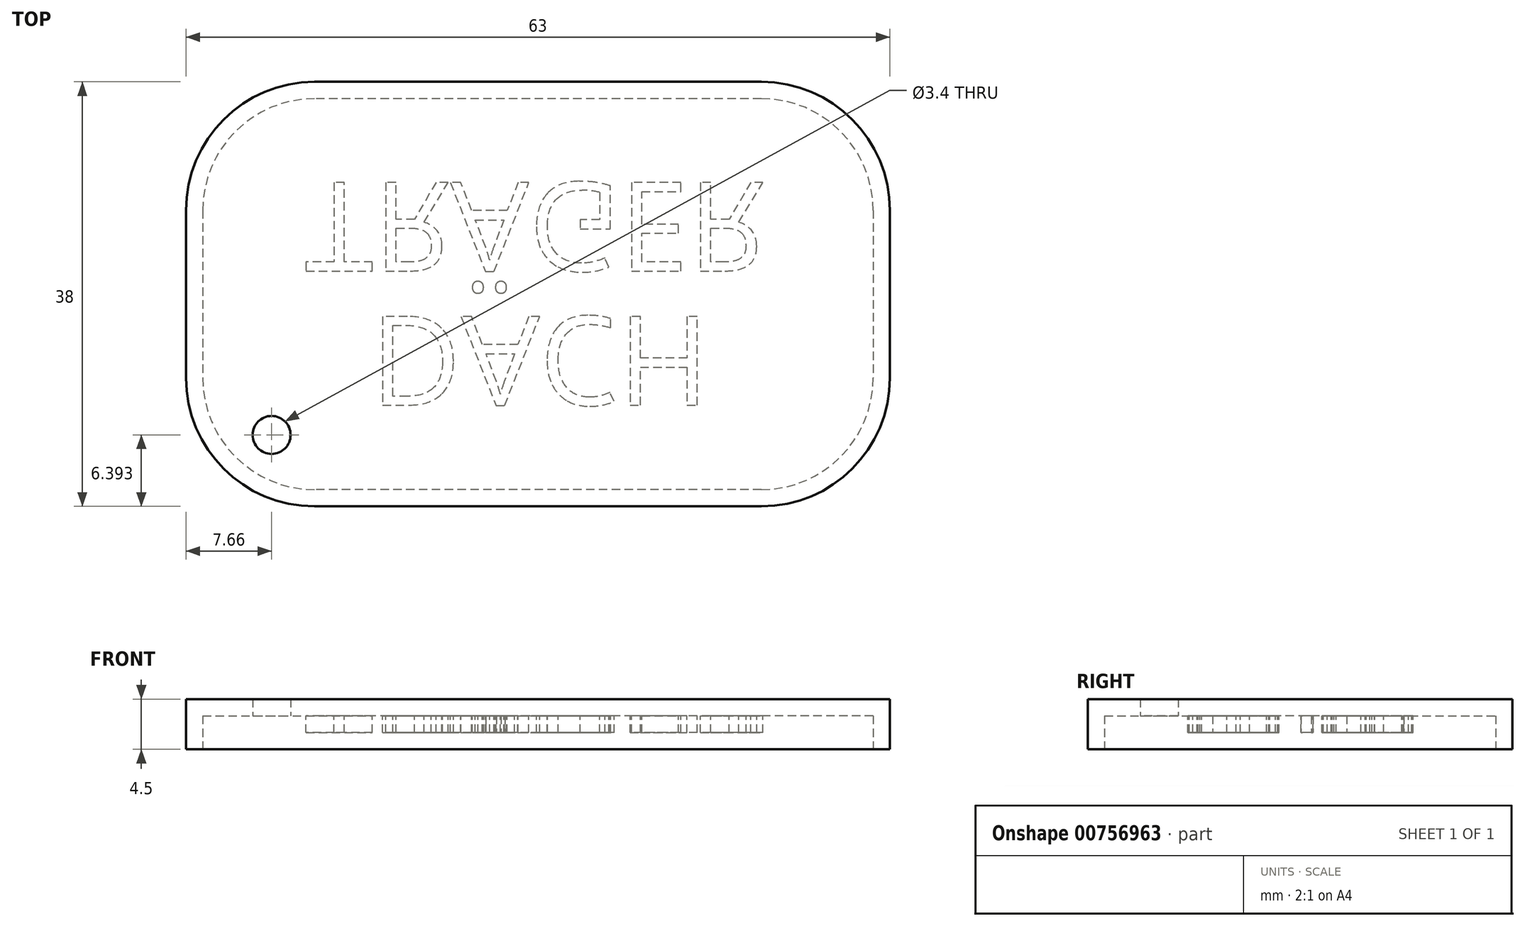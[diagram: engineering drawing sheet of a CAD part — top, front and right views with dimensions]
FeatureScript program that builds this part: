
annotation { "Feature Type Name" : "Feature", "Feature Type Description" : "" }
export const myFeature = defineFeature(function(context is Context, id is Id, definition is map)
    precondition{}
    {
        {
            var Q0;
            Q0=qCreatedBy(makeId("Top.planeOp"),FACE);
            var sketch = newSketch(context, id + "F0", { "sketchPlane" : qUnion([Q0])});
            skLineSegment(sketch, "E0.bottom", {"start": v(30, 17.5) * mm, "end": v(-30, 17.5) * mm});
            skLineSegment(sketch, "E0.top", {"start": v(30, -17.5) * mm, "end": v(-30, -17.5) * mm});
            skLineSegment(sketch, "E0.left", {"start": v(30, 17.5) * mm, "end": v(30, -17.5) * mm});
            skLineSegment(sketch, "E0.right", {"start": v(-30, 17.5) * mm, "end": v(-30, -17.5) * mm});
            skPoint(sketch, "E0.middle", {"position": v(0, 0) * mm});
            skSolve(sketch);
        }
        {
            var Q0;
            Q0=makeQuery(id+"F0.imprint","IMPRINT",FACE,{"disambiguationData":[TD([[makeQuery(id+"F0.imprint","IMPRINT",EDGE,{"derivedFrom":sQuery(id+"F0.wireOp",EDGE,"E0.bottom")}),1.0]])]});
            extrude(context, id + "F1", {"entities" : qUnion([Q0]), "depth" : 3 * mm, "offsetDistance" : 25 * mm});
        }
        {
            var Q0;
            Q0=makeQuery(id+"F1.opExtrude","SWEPT_EDGE",EDGE,{"disambiguationData":[OSD([sQuery(id+"F0.wireOp",EDGE,"E0.bottom"),sQuery(id+"F0.wireOp",EDGE,"E0.left")])]});
            var Q1;
            Q1=makeQuery(id+"F1.opExtrude","SWEPT_EDGE",EDGE,{"disambiguationData":[OSD([sQuery(id+"F0.wireOp",EDGE,"E0.top"),sQuery(id+"F0.wireOp",EDGE,"E0.right")])]});
            var Q2;
            Q2=makeQuery(id+"F1.opExtrude","SWEPT_EDGE",EDGE,{"disambiguationData":[OSD([sQuery(id+"F0.wireOp",EDGE,"E0.top"),sQuery(id+"F0.wireOp",EDGE,"E0.left")])]});
            var Q3;
            Q3=makeQuery(id+"F1.opExtrude","SWEPT_EDGE",EDGE,{"disambiguationData":[OSD([sQuery(id+"F0.wireOp",EDGE,"E0.bottom"),sQuery(id+"F0.wireOp",EDGE,"E0.right")])]});
            fillet(context, id + "F2", {"entities" : qUnion([Q0, Q1, Q2, Q3]), "radius" : 10 * mm, "tangentPropagation" : true, "allowEdgeOverflow" : false});
        }
        {
            var Q0;
            Q0=makeQuery(id+"F1.opExtrude","CAP_FACE",FACE,{"disambiguationData":[OSD([sQuery(id+"F0.wireOp",EDGE,"E0.bottom"),sQuery(id+"F0.wireOp",EDGE,"E0.top"),sQuery(id+"F0.wireOp",EDGE,"E0.left"),sQuery(id+"F0.wireOp",EDGE,"E0.right")])],"isStart":true});
            shell(context, id + "F3", {"entities" : qUnion([Q0]), "thickness" : 1.5 * mm, "oppositeDirection" : true});
        }
        {
            var Q0;
            Q0=makeQuery(id+"F3.opShell","OFFSET_FACE",FACE,{"disambiguationData":[OSD([sQuery(id+"F0.wireOp",EDGE,"E0.bottom"),sQuery(id+"F0.wireOp",EDGE,"E0.top"),sQuery(id+"F0.wireOp",EDGE,"E0.left"),sQuery(id+"F0.wireOp",EDGE,"E0.right")])]});
            var sketch = newSketch(context, id + "F4", { "sketchPlane" : qUnion([Q0])});
            skText(sketch, "E1", { "text": "DACH", "fontName": "OpenSans-Regular.ttf"});
            skText(sketch, "E2", { "text": "TRÄGER", "fontName": "OpenSans-Regular.ttf"});
            const initialGuessF4  = {"E1": [-0.01499, 0.002, 1, 0, 0.008], "E2": [-0.02086, -0.01, 1, 0, 0.008]};
            skSetInitialGuess(sketch, initialGuessF4);
            skSolve(sketch);
        }
        {
            var Q0;
            Q0=qSketchRegion(id+"F4",true);
            extrude(context, id + "F5", {"entities" : qUnion([Q0]), "operationType" : NewBodyOperationType.ADD, "depth" : 1.5 * mm, "offsetDistance" : 25 * mm});
        }
        {
            var Q0;
            {var subQ0=sQuery(id+"F0.wireOp",EDGE,"E0.right");var subQ1=sQuery(id+"F0.wireOp",EDGE,"E0.top");var subQ2=sQuery(id+"F0.wireOp",EDGE,"E0.left");var subQ3=sQuery(id+"F0.wireOp",EDGE,"E0.bottom");Q0=makeQuery(id+"F5.boolean.opBoolean","SPLIT",FACE,{"disambiguationData":[TD([makeQuery(id+"F3.opShell","OFFSET_FACE",FACE,{"disambiguationData":[OSD([subQ3])]})])],"derivedFrom":makeQuery(id+"F3.opShell","OFFSET_FACE",FACE,{"disambiguationData":[OSD([subQ3,subQ1,subQ2,subQ0])]})});}
            var sketch = newSketch(context, id + "F6", { "sketchPlane" : qUnion([Q0])});
            skPoint(sketch, "E3", {"position": v(-23.84, 12.6) * mm});
            skSolve(sketch);
        }
        {
            var Q0;
            Q0=sQuery(id+"F6.wireOp",VERTEX,"E3");
            var Q1;
            Q1=makeQuery(id+"F1.opExtrude","SWEPT_BODY",BODY,{"disambiguationData":[OSD([sQuery(id+"F0.wireOp",EDGE,"E0.bottom"),sQuery(id+"F0.wireOp",EDGE,"E0.top"),sQuery(id+"F0.wireOp",EDGE,"E0.left"),sQuery(id+"F0.wireOp",EDGE,"E0.right")])]});
            hole(context, id + "F7", {"style" : HoleStyle.SIMPLE, "endStyle" : HoleEndStyle.THROUGH, "holeDiameter" : 3.4 * mm, "majorDiameter" : 5 * mm, "isTappedThrough" : true, "tappedDepth" : 12 * mm, "tapClearance" : 3, "locations" : qUnion([Q0]), "scope" : qUnion([Q1])});
        }
    });
